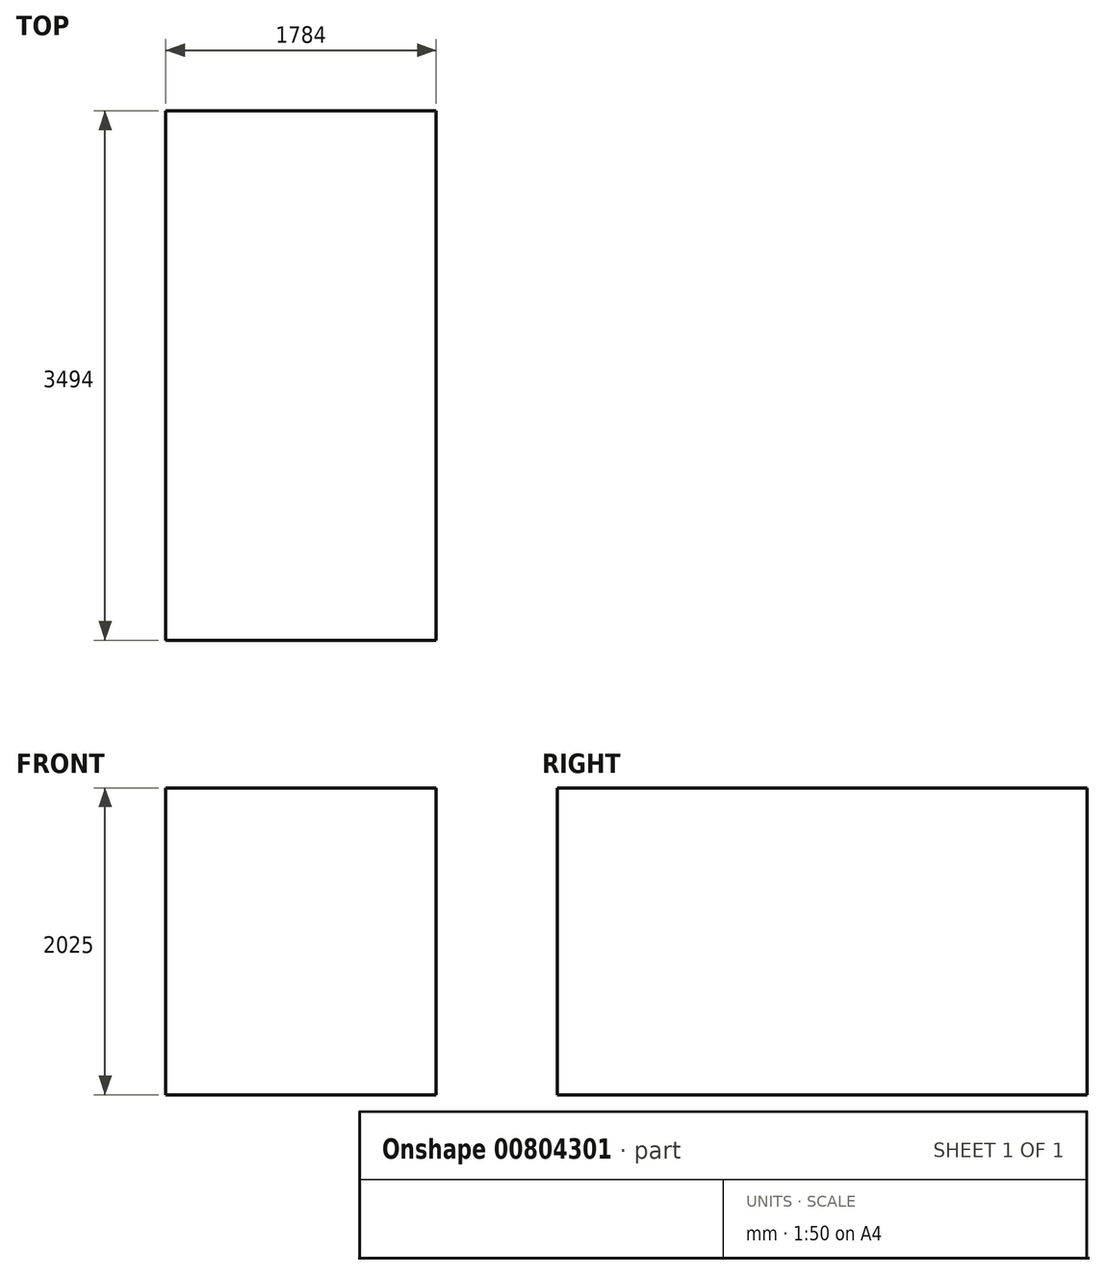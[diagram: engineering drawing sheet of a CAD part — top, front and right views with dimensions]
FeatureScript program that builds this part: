
annotation { "Feature Type Name" : "Feature", "Feature Type Description" : "" }
export const myFeature = defineFeature(function(context is Context, id is Id, definition is map)
    precondition{}
    {
        {
            var Q0;
            Q0=qCreatedBy(makeId("Top.planeOp"),FACE);
            var sketch = newSketch(context, id + "F0", { "sketchPlane" : qUnion([Q0])});
            skLineSegment(sketch, "E0.bottom", {"start": v(-1609.92, 1747.77) * mm, "end": v(174.08, 1747.77) * mm});
            skLineSegment(sketch, "E0.top", {"start": v(-1609.92, -1746.23) * mm, "end": v(174.08, -1746.23) * mm});
            skLineSegment(sketch, "E0.left", {"start": v(-1609.92, 1747.77) * mm, "end": v(-1609.92, -1746.23) * mm});
            skLineSegment(sketch, "E0.right", {"start": v(174.08, 1747.77) * mm, "end": v(174.08, -1746.23) * mm});
            skSolve(sketch);
        }
        {
            var Q0;
            Q0 = qSketchRegion(id + "F0", true);
            var Q1;
            Q1=makeQuery(id+"F0.imprint","IMPRINT",FACE,{"disambiguationData":[TD([[makeQuery(id+"F0.imprint","IMPRINT",EDGE,{"derivedFrom":sQuery(id+"F0.wireOp",EDGE,"E0.bottom")}),-1.0]])]});
            extrude(context, id + "F1", {"entities" : qUnion([Q0, Q1]), "depth" : 2025 * mm, "offsetDistance" : 25 * mm});
        }
    });
